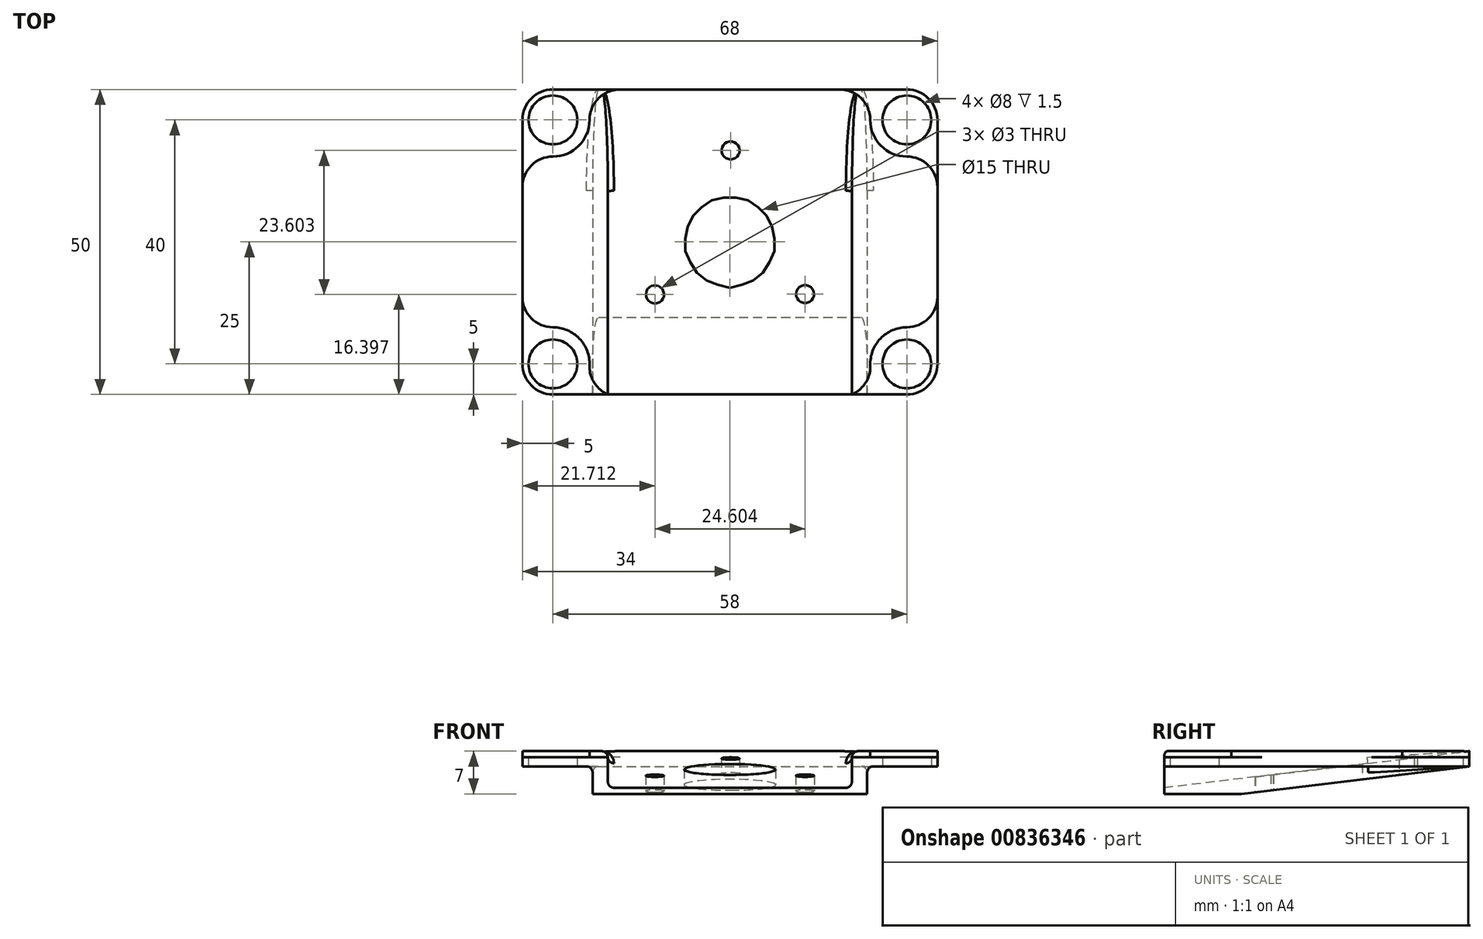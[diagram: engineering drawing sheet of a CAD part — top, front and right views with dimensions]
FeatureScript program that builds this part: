
annotation { "Feature Type Name" : "Feature", "Feature Type Description" : "" }
export const myFeature = defineFeature(function(context is Context, id is Id, definition is map)
    precondition{}
    {
        {
            var Q0;
            Q0=qCreatedBy(makeId("Right.planeOp"),FACE);
            var sketch = newSketch(context, id + "F0", { "sketchPlane" : qUnion([Q0])});
            skLineSegment(sketch, "E0", {"start": v(-25, 0) * mm, "end": v(25, 0) * mm});
            skLineSegment(sketch, "E1", {"start": v(25, 0) * mm, "end": v(25, 8) * mm});
            skLineSegment(sketch, "E2", {"start": v(-25, 8) * mm, "end": v(-25, 0) * mm});
            skLineSegment(sketch, "E3", {"start": v(25, 8) * mm, "end": v(-25, 8) * mm});
            skSolve(sketch);
        }
        {
            var Q0;
            Q0=makeQuery(id+"F0.imprint","IMPRINT",FACE,{"disambiguationData":[TD([[makeQuery(id+"F0.imprint","IMPRINT",EDGE,{"derivedFrom":sQuery(id+"F0.wireOp",EDGE,"E0")}),1.0]])]});
            extrude(context, id + "F1", {"entities" : qUnion([Q0]), "endBound" : BoundingType.SYMMETRIC, "depth" : 68 * mm, "offsetDistance" : 25 * mm});
        }
        {
            var Q0;
            Q0=qCreatedBy(makeId("Right.planeOp"),FACE);
            var sketch = newSketch(context, id + "F2", { "sketchPlane" : qUnion([Q0])});
            skLineSegment(sketch, "E4", {"start": v(25, 8) * mm, "end": v(-25, 2) * mm});
            skLineSegment(sketch, "E5", {"start": v(-25, 2) * mm, "end": v(-25, 14.14) * mm});
            skLineSegment(sketch, "E6", {"start": v(-25, 14.14) * mm, "end": v(25, 14.14) * mm});
            skLineSegment(sketch, "E7", {"start": v(25, 14.14) * mm, "end": v(25, 8) * mm});
            skSolve(sketch);
        }
        {
            var Q0;
            Q0=makeQuery(id+"F2.imprint","IMPRINT",FACE,{"disambiguationData":[TD([[makeQuery(id+"F2.imprint","IMPRINT",EDGE,{"derivedFrom":sQuery(id+"F2.wireOp",EDGE,"E4")}),-1.0]])]});
            extrude(context, id + "F3", {"entities" : qUnion([Q0]), "operationType" : NewBodyOperationType.REMOVE, "endBound" : BoundingType.SYMMETRIC, "oppositeDirection" : true, "depth" : 40 * mm, "offsetDistance" : 25 * mm});
        }
        {
            var Q0;
            Q0=makeQuery(id+"F1.opExtrude","SWEPT_FACE",FACE,{"disambiguationData":[OSD([sQuery(id+"F0.wireOp",EDGE,"E0")])]});
            var Q1;
            Q1=makeQuery(id+"F1.opExtrude","CAP_FACE",FACE,{"disambiguationData":[OSD([sQuery(id+"F0.wireOp",EDGE,"E0"),sQuery(id+"F0.wireOp",EDGE,"E1"),sQuery(id+"F0.wireOp",EDGE,"E2"),sQuery(id+"F0.wireOp",EDGE,"E3")])],"isStart":true});
            var Q2;
            Q2=makeQuery(id+"F1.opExtrude","CAP_FACE",FACE,{"disambiguationData":[OSD([sQuery(id+"F0.wireOp",EDGE,"E0"),sQuery(id+"F0.wireOp",EDGE,"E1"),sQuery(id+"F0.wireOp",EDGE,"E2"),sQuery(id+"F0.wireOp",EDGE,"E3")])],"isStart":false});
            var Q3;
            Q3=makeQuery(id+"F1.opExtrude","SWEPT_FACE",FACE,{"disambiguationData":[OSD([sQuery(id+"F0.wireOp",EDGE,"E2")])]});
            var Q4;
            Q4=makeQuery(id+"F1.opExtrude","SWEPT_FACE",FACE,{"disambiguationData":[OSD([sQuery(id+"F0.wireOp",EDGE,"E1")])]});
            shell(context, id + "F4", {"entities" : qUnion([Q0, Q1, Q2, Q3, Q4]), "thickness" : 2.5 * mm});
        }
        {
            var Q0;
            Q0=qCreatedBy(makeId("Top.planeOp"),FACE);
            var sketch = newSketch(context, id + "F5", { "sketchPlane" : qUnion([Q0])});
            skCircle(sketch, "E8", {"center": v(0, 0) * mm, "radius": 7.5 * mm});
            skCircle(sketch, "E9", {"center": v(-29, 20) * mm, "radius": 4 * mm});
            skCircle(sketch, "E10", {"center": v(-29, -20) * mm, "radius": 4 * mm});
            skCircle(sketch, "E11", {"center": v(29, -20) * mm, "radius": 4 * mm});
            skCircle(sketch, "E12", {"center": v(29, 20) * mm, "radius": 4 * mm});
            skCircle(sketch, "E13", {"center": v(0.1, 15) * mm, "radius": 1.5 * mm});
            skCircle(sketch, "E14", {"center": v(12.32, -8.56) * mm, "radius": 1.5 * mm});
            skCircle(sketch, "E15", {"center": v(-12.29, -8.6) * mm, "radius": 1.5 * mm});
            skSolve(sketch);
        }
        {
            var Q0;
            Q0=qSketchRegion(id+"F5",true);
            extrude(context, id + "F6", {"entities" : qUnion([Q0]), "operationType" : NewBodyOperationType.REMOVE, "depth" : 25 * mm, "offsetDistance" : 25 * mm});
        }
        {
            var Q0;
            Q0=makeQuery(id+"F1.opExtrude","CAP_EDGE",EDGE,{"disambiguationData":[OSD([sQuery(id+"F0.wireOp",EDGE,"E2")])],"isStart":false});
            var Q1;
            Q1=makeQuery(id+"F1.opExtrude","CAP_EDGE",EDGE,{"disambiguationData":[OSD([sQuery(id+"F0.wireOp",EDGE,"E1")])],"isStart":false});
            var Q2;
            Q2=makeQuery(id+"F1.opExtrude","CAP_EDGE",EDGE,{"disambiguationData":[OSD([sQuery(id+"F0.wireOp",EDGE,"E2")])],"isStart":true});
            var Q3;
            Q3=makeQuery(id+"F1.opExtrude","CAP_EDGE",EDGE,{"disambiguationData":[OSD([sQuery(id+"F0.wireOp",EDGE,"E1")])],"isStart":true});
            fillet(context, id + "F7", {"entities" : qUnion([Q0, Q1, Q2, Q3]), "radius" : 5 * mm, "tangentPropagation" : true, "allowEdgeOverflow" : false});
        }
        {
            var Q0;
            Q0=makeQuery(id+"F3.boolean.opBoolean","INTERSECT",EDGE,{"derivedFrom":[makeQuery(id+"F1.opExtrude","SWEPT_FACE",FACE,{"disambiguationData":[OSD([sQuery(id+"F0.wireOp",EDGE,"E3")])]}),makeQuery(id+"F3.opExtrude","CAP_FACE",FACE,{"disambiguationData":[OSD([sQuery(id+"F2.wireOp",EDGE,"E4"),sQuery(id+"F2.wireOp",EDGE,"E5"),sQuery(id+"F2.wireOp",EDGE,"E6"),sQuery(id+"F2.wireOp",EDGE,"E7")])],"isStart":false})]});
            var Q1;
            Q1=makeQuery(id+"F3.boolean.opBoolean","INTERSECT",EDGE,{"derivedFrom":[makeQuery(id+"F1.opExtrude","SWEPT_FACE",FACE,{"disambiguationData":[OSD([sQuery(id+"F0.wireOp",EDGE,"E3")])]}),makeQuery(id+"F3.opExtrude","CAP_FACE",FACE,{"disambiguationData":[OSD([sQuery(id+"F2.wireOp",EDGE,"E4"),sQuery(id+"F2.wireOp",EDGE,"E5"),sQuery(id+"F2.wireOp",EDGE,"E6"),sQuery(id+"F2.wireOp",EDGE,"E7")])],"isStart":true})]});
            var Q2;
            {var subQ0=sQuery(id+"F2.wireOp",EDGE,"E4");Q2=makeQuery(id+"F4.opShell","OFFSET_EDGE",EDGE,{"disambiguationData":[OSD([subQ0]),TDD([makeQuery(id+"F3.boolean.opBoolean","COPY",EDGE,{"derivedFrom":makeQuery(id+"F3.opExtrude","CAP_EDGE",EDGE,{"disambiguationData":[OSD([subQ0])],"isStart":true})})])]});}
            var Q3;
            {var subQ0=sQuery(id+"F2.wireOp",EDGE,"E4");Q3=makeQuery(id+"F4.opShell","OFFSET_EDGE",EDGE,{"disambiguationData":[OSD([subQ0]),TDD([makeQuery(id+"F3.boolean.opBoolean","COPY",EDGE,{"derivedFrom":makeQuery(id+"F3.opExtrude","CAP_EDGE",EDGE,{"disambiguationData":[OSD([subQ0])],"isStart":false})})])]});}
            fillet(context, id + "F8", {"entities" : qUnion([Q0, Q1, Q2, Q3]), "radius" : 1 * mm, "tangentPropagation" : true, "allowEdgeOverflow" : false});
        }
        {
            var Q0;
            Q0=makeQuery(id+"F3.boolean.opBoolean","COPY",EDGE,{"derivedFrom":makeQuery(id+"F3.opExtrude","CAP_EDGE",EDGE,{"disambiguationData":[OSD([sQuery(id+"F2.wireOp",EDGE,"E4")])],"isStart":false})});
            var Q1;
            Q1=makeQuery(id+"F3.boolean.opBoolean","COPY",EDGE,{"derivedFrom":makeQuery(id+"F3.opExtrude","CAP_EDGE",EDGE,{"disambiguationData":[OSD([sQuery(id+"F2.wireOp",EDGE,"E4")])],"isStart":true})});
            var Q2;
            {var subQ0=sQuery(id+"F2.wireOp",EDGE,"E7");var subQ1=sQuery(id+"F2.wireOp",EDGE,"E6");var subQ2=sQuery(id+"F2.wireOp",EDGE,"E5");var subQ3=sQuery(id+"F2.wireOp",EDGE,"E4");var subQ4=sQuery(id+"F0.wireOp",EDGE,"E3");Q2=makeQuery(id+"F4.opShell","OFFSET_EDGE",EDGE,{"disambiguationData":[OSD([subQ4,subQ3,subQ2,subQ1,subQ0]),TDD([makeQuery(id+"F3.boolean.opBoolean","INTERSECT",EDGE,{"derivedFrom":[makeQuery(id+"F1.opExtrude","SWEPT_FACE",FACE,{"disambiguationData":[OSD([subQ4])]}),makeQuery(id+"F3.opExtrude","CAP_FACE",FACE,{"disambiguationData":[OSD([subQ3,subQ2,subQ1,subQ0])],"isStart":false})]})])]});}
            var Q3;
            {var subQ0=sQuery(id+"F2.wireOp",EDGE,"E7");var subQ1=sQuery(id+"F2.wireOp",EDGE,"E6");var subQ2=sQuery(id+"F2.wireOp",EDGE,"E5");var subQ3=sQuery(id+"F2.wireOp",EDGE,"E4");var subQ4=sQuery(id+"F0.wireOp",EDGE,"E3");Q3=makeQuery(id+"F4.opShell","OFFSET_EDGE",EDGE,{"disambiguationData":[OSD([subQ4,subQ3,subQ2,subQ1,subQ0]),TDD([makeQuery(id+"F3.boolean.opBoolean","INTERSECT",EDGE,{"derivedFrom":[makeQuery(id+"F1.opExtrude","SWEPT_FACE",FACE,{"disambiguationData":[OSD([subQ4])]}),makeQuery(id+"F3.opExtrude","CAP_FACE",FACE,{"disambiguationData":[OSD([subQ3,subQ2,subQ1,subQ0])],"isStart":true})]})])]});}
            fillet(context, id + "F9", {"entities" : qUnion([Q0, Q1, Q2, Q3]), "radius" : 1 * mm, "tangentPropagation" : true, "allowEdgeOverflow" : false});
        }
        {
            var Q0;
            Q0=qCreatedBy(makeId("Right.planeOp"),FACE);
            var sketch = newSketch(context, id + "F10", { "sketchPlane" : qUnion([Q0])});
            skLineSegment(sketch, "E16.bottom", {"start": v(-40, 0) * mm, "end": v(40, 0) * mm});
            skLineSegment(sketch, "E16.top", {"start": v(-40, 1) * mm, "end": v(40, 1) * mm});
            skLineSegment(sketch, "E16.left", {"start": v(-40, 0) * mm, "end": v(-40, 1) * mm});
            skLineSegment(sketch, "E16.right", {"start": v(40, 0) * mm, "end": v(40, 1) * mm});
            skSolve(sketch);
        }
        {
            var Q0;
            Q0=makeQuery(id+"F10.imprint","IMPRINT",FACE,{"disambiguationData":[TD([[makeQuery(id+"F10.imprint","IMPRINT",EDGE,{"derivedFrom":sQuery(id+"F10.wireOp",EDGE,"E16.bottom")}),1.0]])]});
            extrude(context, id + "F11", {"entities" : qUnion([Q0]), "operationType" : NewBodyOperationType.REMOVE, "endBound" : BoundingType.SYMMETRIC, "oppositeDirection" : true, "depth" : 200 * mm, "offsetDistance" : 25 * mm});
        }
        {
            var Q0;
            {var subQ0=sQuery(id+"F0.wireOp",EDGE,"E2");var subQ2=sQuery(id+"F0.wireOp",EDGE,"E3");var subQ3=sQuery(id+"F0.wireOp",EDGE,"E1");Q0=makeQuery(id+"F3.boolean.opBoolean","SPLIT",FACE,{"disambiguationData":[TD([makeQuery(id+"F1.opExtrude","CAP_FACE",FACE,{"disambiguationData":[OSD([sQuery(id+"F0.wireOp",EDGE,"E0"),subQ3,subQ0,subQ2])],"isStart":true})])],"derivedFrom":makeQuery(id+"F1.opExtrude","SWEPT_FACE",FACE,{"disambiguationData":[OSD([subQ2])]})});}
            var sketch = newSketch(context, id + "F12", { "sketchPlane" : qUnion([Q0])});
            skCircle(sketch, "E17", {"center": v(-29, -20) * mm, "radius": 6 * mm});
            skCircle(sketch, "E18", {"center": v(29, -20) * mm, "radius": 6 * mm});
            skCircle(sketch, "E19", {"center": v(29, 20) * mm, "radius": 6 * mm});
            skCircle(sketch, "E20", {"center": v(-29, 20) * mm, "radius": 6 * mm});
            skSolve(sketch);
        }
        {
            var Q0;
            Q0=qSketchRegion(id+"F12",true);
            extrude(context, id + "F13", {"entities" : qUnion([Q0]), "operationType" : NewBodyOperationType.REMOVE, "oppositeDirection" : true, "depth" : 1 * mm, "offsetDistance" : 25 * mm});
        }
        {
            var Q0;
            Q0=makeQuery(id+"F13.boolean.opBoolean","INTERSECT",EDGE,{"derivedFrom":[makeQuery(id+"F1.opExtrude","SWEPT_FACE",FACE,{"disambiguationData":[OSD([sQuery(id+"F0.wireOp",EDGE,"E2")])]}),makeQuery(id+"F13.opExtrude","SWEPT_FACE",FACE,{"disambiguationData":[OSD([sQuery(id+"F12.wireOp",EDGE,"E17")])]})]});
            var Q1;
            Q1=makeQuery(id+"F13.boolean.opBoolean","INTERSECT",EDGE,{"derivedFrom":[makeQuery(id+"F1.opExtrude","CAP_FACE",FACE,{"disambiguationData":[OSD([sQuery(id+"F0.wireOp",EDGE,"E0"),sQuery(id+"F0.wireOp",EDGE,"E1"),sQuery(id+"F0.wireOp",EDGE,"E2"),sQuery(id+"F0.wireOp",EDGE,"E3")])],"isStart":true}),makeQuery(id+"F13.opExtrude","SWEPT_FACE",FACE,{"disambiguationData":[OSD([sQuery(id+"F12.wireOp",EDGE,"E17")])]})]});
            var Q2;
            Q2=makeQuery(id+"F13.boolean.opBoolean","INTERSECT",EDGE,{"derivedFrom":[makeQuery(id+"F1.opExtrude","SWEPT_FACE",FACE,{"disambiguationData":[OSD([sQuery(id+"F0.wireOp",EDGE,"E2")])]}),makeQuery(id+"F13.opExtrude","SWEPT_FACE",FACE,{"disambiguationData":[OSD([sQuery(id+"F12.wireOp",EDGE,"E18")])]})]});
            var Q3;
            Q3=makeQuery(id+"F13.boolean.opBoolean","INTERSECT",EDGE,{"derivedFrom":[makeQuery(id+"F1.opExtrude","CAP_FACE",FACE,{"disambiguationData":[OSD([sQuery(id+"F0.wireOp",EDGE,"E0"),sQuery(id+"F0.wireOp",EDGE,"E1"),sQuery(id+"F0.wireOp",EDGE,"E2"),sQuery(id+"F0.wireOp",EDGE,"E3")])],"isStart":false}),makeQuery(id+"F13.opExtrude","SWEPT_FACE",FACE,{"disambiguationData":[OSD([sQuery(id+"F12.wireOp",EDGE,"E18")])]})]});
            var Q4;
            Q4=makeQuery(id+"F13.boolean.opBoolean","INTERSECT",EDGE,{"derivedFrom":[makeQuery(id+"F1.opExtrude","CAP_FACE",FACE,{"disambiguationData":[OSD([sQuery(id+"F0.wireOp",EDGE,"E0"),sQuery(id+"F0.wireOp",EDGE,"E1"),sQuery(id+"F0.wireOp",EDGE,"E2"),sQuery(id+"F0.wireOp",EDGE,"E3")])],"isStart":false}),makeQuery(id+"F13.opExtrude","SWEPT_FACE",FACE,{"disambiguationData":[OSD([sQuery(id+"F12.wireOp",EDGE,"E19")])]})]});
            var Q5;
            Q5=makeQuery(id+"F13.boolean.opBoolean","INTERSECT",EDGE,{"derivedFrom":[makeQuery(id+"F1.opExtrude","SWEPT_FACE",FACE,{"disambiguationData":[OSD([sQuery(id+"F0.wireOp",EDGE,"E1")])]}),makeQuery(id+"F13.opExtrude","SWEPT_FACE",FACE,{"disambiguationData":[OSD([sQuery(id+"F12.wireOp",EDGE,"E19")])]})]});
            var Q6;
            Q6=makeQuery(id+"F13.boolean.opBoolean","INTERSECT",EDGE,{"derivedFrom":[makeQuery(id+"F1.opExtrude","SWEPT_FACE",FACE,{"disambiguationData":[OSD([sQuery(id+"F0.wireOp",EDGE,"E1")])]}),makeQuery(id+"F13.opExtrude","SWEPT_FACE",FACE,{"disambiguationData":[OSD([sQuery(id+"F12.wireOp",EDGE,"E20")])]})]});
            var Q7;
            Q7=makeQuery(id+"F13.boolean.opBoolean","INTERSECT",EDGE,{"derivedFrom":[makeQuery(id+"F1.opExtrude","CAP_FACE",FACE,{"disambiguationData":[OSD([sQuery(id+"F0.wireOp",EDGE,"E0"),sQuery(id+"F0.wireOp",EDGE,"E1"),sQuery(id+"F0.wireOp",EDGE,"E2"),sQuery(id+"F0.wireOp",EDGE,"E3")])],"isStart":true}),makeQuery(id+"F13.opExtrude","SWEPT_FACE",FACE,{"disambiguationData":[OSD([sQuery(id+"F12.wireOp",EDGE,"E20")])]})]});
            fillet(context, id + "F14", {"entities" : qUnion([Q0, Q1, Q2, Q3, Q4, Q5, Q6, Q7]), "radius" : 5 * mm, "tangentPropagation" : true, "allowEdgeOverflow" : false});
        }
    });
